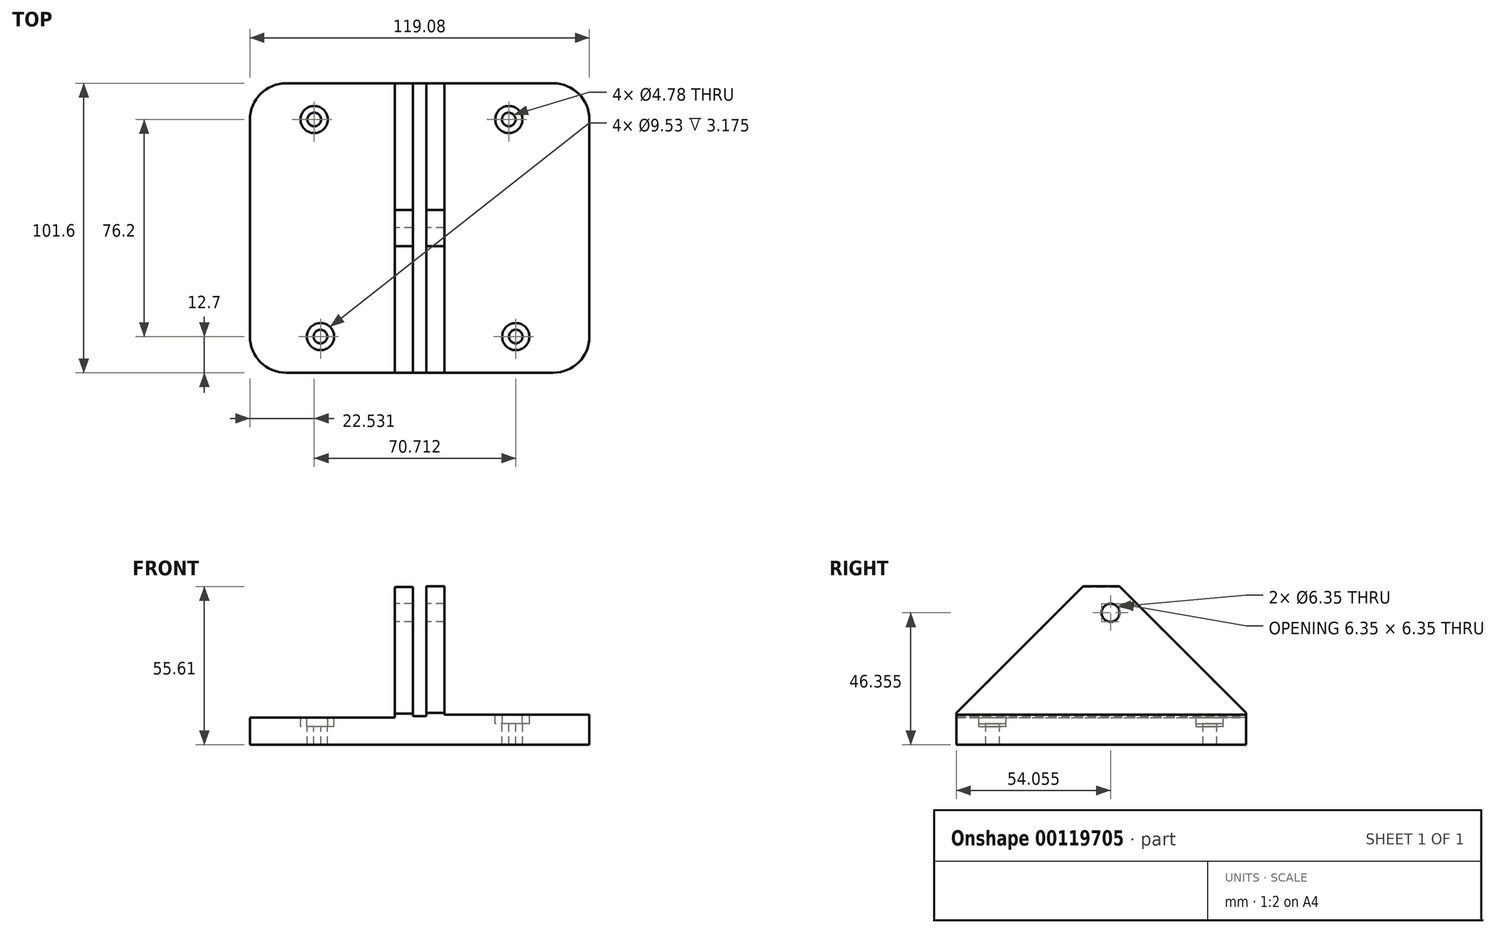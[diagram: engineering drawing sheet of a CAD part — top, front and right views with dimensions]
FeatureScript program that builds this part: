
annotation { "Feature Type Name" : "Feature", "Feature Type Description" : "" }
export const myFeature = defineFeature(function(context is Context, id is Id, definition is map)
    precondition{}
    {
        {
            var Q0;
            Q0=qCreatedBy(makeId("Front.planeOp"),FACE);
            var sketch = newSketch(context, id + "F0", { "sketchPlane" : qUnion([Q0])});
            skLineSegment(sketch, "E0", {"start": v(0, 0) * mm, "end": v(0, 9.53) * mm});
            skLineSegment(sketch, "E1", {"start": v(0, 9.53) * mm, "end": v(50.8, 9.53) * mm});
            skLineSegment(sketch, "E2", {"start": v(50.8, 9.53) * mm, "end": v(50.8, 55.4) * mm});
            skLineSegment(sketch, "E3", {"start": v(50.8, 55.4) * mm, "end": v(57.15, 55.4) * mm});
            skLineSegment(sketch, "E4", {"start": v(57.15, 55.4) * mm, "end": v(57.15, 10.14) * mm});
            skLineSegment(sketch, "E5", {"start": v(57.15, 10.14) * mm, "end": v(61.93, 10.14) * mm});
            skLineSegment(sketch, "E6", {"start": v(61.93, 10.14) * mm, "end": v(61.93, 55.61) * mm});
            skLineSegment(sketch, "E7", {"start": v(61.93, 55.61) * mm, "end": v(68.28, 55.61) * mm});
            skLineSegment(sketch, "E8", {"start": v(68.28, 55.61) * mm, "end": v(68.28, 10.55) * mm});
            skLineSegment(sketch, "E9", {"start": v(68.28, 10.55) * mm, "end": v(119.08, 10.55) * mm});
            skLineSegment(sketch, "E10", {"start": v(119.08, 10.55) * mm, "end": v(119.08, 0) * mm});
            skLineSegment(sketch, "E11", {"start": v(119.08, 0) * mm, "end": v(0, 0) * mm});
            skSolve(sketch);
        }
        {
            var Q0;
            Q0 = qSketchRegion(id + "F0", true);
            extrude(context, id + "F1", {"entities" : qUnion([Q0]), "depth" : 101.6 * mm});
        }
        {
            var Q0;
            Q0=makeQuery(id+"F1.opExtrude","SWEPT_FACE",FACE,{"disambiguationData":[OSD([sQuery(id+"F0.wireOp",EDGE,"E1")])]});
            var sketch = newSketch(context, id + "F2", { "sketchPlane" : qUnion([Q0])});
            skPoint(sketch, "E12", {"position": v(22.53, -12.7) * mm});
            skPoint(sketch, "E13", {"position": v(24.76, -88.9) * mm});
            skSolve(sketch);
        }
        {
            var Q0;
            Q0=sQuery(id+"F2.wireOp",VERTEX,"E12");
            var Q1;
            Q1=sQuery(id+"F2.wireOp",VERTEX,"E13");
            var Q2;
            Q2=makeQuery(id+"F1.opExtrude","SWEPT_BODY",BODY,{"disambiguationData":[OSD([sQuery(id+"F0.wireOp",EDGE,"E0"),sQuery(id+"F0.wireOp",EDGE,"E1"),sQuery(id+"F0.wireOp",EDGE,"E2"),sQuery(id+"F0.wireOp",EDGE,"E3"),sQuery(id+"F0.wireOp",EDGE,"E4"),sQuery(id+"F0.wireOp",EDGE,"E5"),sQuery(id+"F0.wireOp",EDGE,"E6"),sQuery(id+"F0.wireOp",EDGE,"E7"),sQuery(id+"F0.wireOp",EDGE,"E8"),sQuery(id+"F0.wireOp",EDGE,"E9"),sQuery(id+"F0.wireOp",EDGE,"E10"),sQuery(id+"F0.wireOp",EDGE,"E11")])]});
            hole(context, id + "F3", {"style" : HoleStyle.C_BORE, "endStyle" : HoleEndStyle.THROUGH, "holeDiameter" : 4.78 * mm, "cBoreDiameter" : 9.52 * mm, "cBoreDepth" : 3.17 * mm, "locations" : qUnion([Q0, Q1]), "scope" : qUnion([Q2]), "isTappedThrough" : true});
        }
        {
            var Q0;
            Q0=makeQuery(id+"F1.opExtrude","SWEPT_FACE",FACE,{"disambiguationData":[OSD([sQuery(id+"F0.wireOp",EDGE,"E9")])]});
            var sketch = newSketch(context, id + "F4", { "sketchPlane" : qUnion([Q0])});
            skPoint(sketch, "E14", {"position": v(90.8, -12.7) * mm});
            skPoint(sketch, "E15", {"position": v(93.24, -88.9) * mm});
            skSolve(sketch);
        }
        {
            var Q0;
            Q0=sQuery(id+"F4.wireOp",VERTEX,"E14");
            var Q1;
            Q1=sQuery(id+"F4.wireOp",VERTEX,"E15");
            var Q2;
            Q2=makeQuery(id+"F1.opExtrude","SWEPT_BODY",BODY,{"disambiguationData":[OSD([sQuery(id+"F0.wireOp",EDGE,"E0"),sQuery(id+"F0.wireOp",EDGE,"E1"),sQuery(id+"F0.wireOp",EDGE,"E2"),sQuery(id+"F0.wireOp",EDGE,"E3"),sQuery(id+"F0.wireOp",EDGE,"E4"),sQuery(id+"F0.wireOp",EDGE,"E5"),sQuery(id+"F0.wireOp",EDGE,"E6"),sQuery(id+"F0.wireOp",EDGE,"E7"),sQuery(id+"F0.wireOp",EDGE,"E8"),sQuery(id+"F0.wireOp",EDGE,"E9"),sQuery(id+"F0.wireOp",EDGE,"E10"),sQuery(id+"F0.wireOp",EDGE,"E11")])]});
            hole(context, id + "F5", {"style" : HoleStyle.C_BORE, "endStyle" : HoleEndStyle.THROUGH, "holeDiameter" : 4.78 * mm, "cBoreDiameter" : 9.52 * mm, "cBoreDepth" : 3.17 * mm, "locations" : qUnion([Q0, Q1]), "scope" : qUnion([Q2]), "isTappedThrough" : true});
        }
        {
            var Q0;
            Q0=makeQuery(id+"F1.opExtrude","SWEPT_FACE",FACE,{"disambiguationData":[OSD([sQuery(id+"F0.wireOp",EDGE,"E2")])]});
            var sketch = newSketch(context, id + "F6", { "sketchPlane" : qUnion([Q0])});
            skPoint(sketch, "E16", {"position": v(47.54, 46.35) * mm});
            skSolve(sketch);
        }
        {
            var Q0;
            Q0=sQuery(id+"F6.wireOp",VERTEX,"E16");
            var Q1;
            Q1=makeQuery(id+"F1.opExtrude","SWEPT_BODY",BODY,{"disambiguationData":[OSD([sQuery(id+"F0.wireOp",EDGE,"E0"),sQuery(id+"F0.wireOp",EDGE,"E1"),sQuery(id+"F0.wireOp",EDGE,"E2"),sQuery(id+"F0.wireOp",EDGE,"E3"),sQuery(id+"F0.wireOp",EDGE,"E4"),sQuery(id+"F0.wireOp",EDGE,"E5"),sQuery(id+"F0.wireOp",EDGE,"E6"),sQuery(id+"F0.wireOp",EDGE,"E7"),sQuery(id+"F0.wireOp",EDGE,"E8"),sQuery(id+"F0.wireOp",EDGE,"E9"),sQuery(id+"F0.wireOp",EDGE,"E10"),sQuery(id+"F0.wireOp",EDGE,"E11")])]});
            hole(context, id + "F7", {"style" : HoleStyle.SIMPLE, "endStyle" : HoleEndStyle.THROUGH, "holeDiameter" : 6.35 * mm, "locations" : qUnion([Q0]), "scope" : qUnion([Q1]), "isTappedThrough" : true});
        }
        {
            var Q0;
            Q0=makeQuery(id+"F1.opExtrude","CAP_EDGE",EDGE,{"disambiguationData":[OSD([sQuery(id+"F0.wireOp",EDGE,"E3")])],"isStart":true});
            var Q1;
            Q1=makeQuery(id+"F1.opExtrude","CAP_EDGE",EDGE,{"disambiguationData":[OSD([sQuery(id+"F0.wireOp",EDGE,"E3")])],"isStart":false});
            var Q2;
            Q2=makeQuery(id+"F1.opExtrude","CAP_EDGE",EDGE,{"disambiguationData":[OSD([sQuery(id+"F0.wireOp",EDGE,"E7")])],"isStart":false});
            var Q3;
            Q3=makeQuery(id+"F1.opExtrude","CAP_EDGE",EDGE,{"disambiguationData":[OSD([sQuery(id+"F0.wireOp",EDGE,"E7")])],"isStart":true});
            chamfer(context, id + "F8", {"entities" : qUnion([Q0, Q1, Q2, Q3]), "width" : 44.45 * mm, "tangentPropagation" : true});
        }
        {
            var Q0;
            Q0=makeQuery(id+"F1.opExtrude","CAP_EDGE",EDGE,{"disambiguationData":[OSD([sQuery(id+"F0.wireOp",EDGE,"E0")])],"isStart":true});
            var Q1;
            Q1=makeQuery(id+"F1.opExtrude","CAP_EDGE",EDGE,{"disambiguationData":[OSD([sQuery(id+"F0.wireOp",EDGE,"E0")])],"isStart":false});
            var Q2;
            Q2=makeQuery(id+"F1.opExtrude","CAP_EDGE",EDGE,{"disambiguationData":[OSD([sQuery(id+"F0.wireOp",EDGE,"E10")])],"isStart":false});
            var Q3;
            Q3=makeQuery(id+"F1.opExtrude","CAP_EDGE",EDGE,{"disambiguationData":[OSD([sQuery(id+"F0.wireOp",EDGE,"E10")])],"isStart":true});
            fillet(context, id + "F9", {"entities" : qUnion([Q0, Q1, Q2, Q3]), "radius" : 12.7 * mm, "tangentPropagation" : true, "allowEdgeOverflow" : false});
        }
    });
